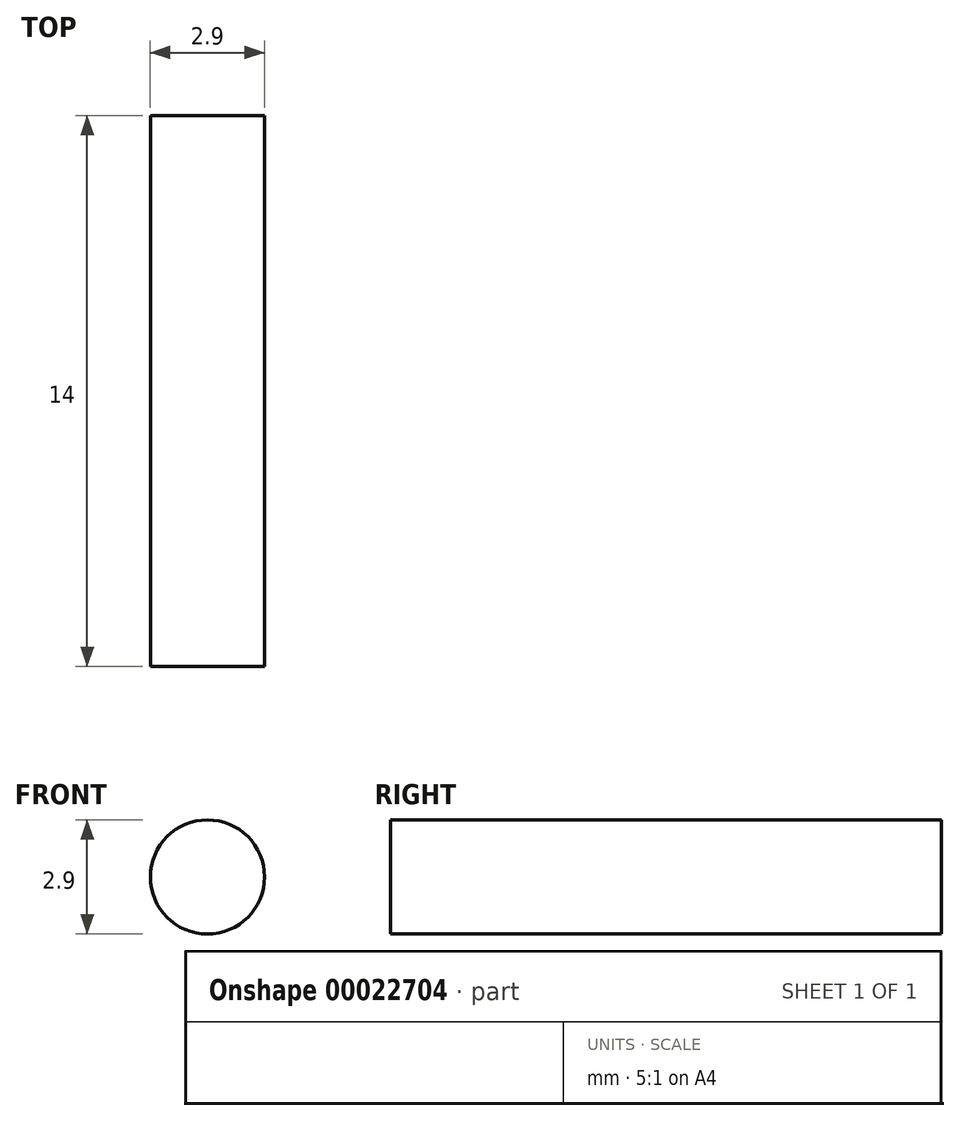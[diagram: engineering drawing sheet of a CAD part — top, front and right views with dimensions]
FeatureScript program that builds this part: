
annotation { "Feature Type Name" : "Feature", "Feature Type Description" : "" }
export const myFeature = defineFeature(function(context is Context, id is Id, definition is map)
    precondition{}
    {
        {
            var Q0;
            Q0=qCreatedBy(makeId("Front.planeOp"),FACE);
            var sketch = newSketch(context, id + "F0", { "sketchPlane" : qUnion([Q0])});
            skCircle(sketch, "E0", {"center": v(-20.65, 12.6) * mm, "radius": 1.45 * mm});
            skSolve(sketch);
        }
        {
            var Q0;
            Q0=makeQuery(id+"F0.imprint","IMPRINT",FACE,{"disambiguationData":[TD([[makeQuery(id+"F0.imprint","IMPRINT",EDGE,{"derivedFrom":sQuery(id+"F0.wireOp",EDGE,"E0")}),1.0]])]});
            extrude(context, id + "F1", {"entities" : qUnion([Q0]), "depth" : 14 * mm});
        }
    });
